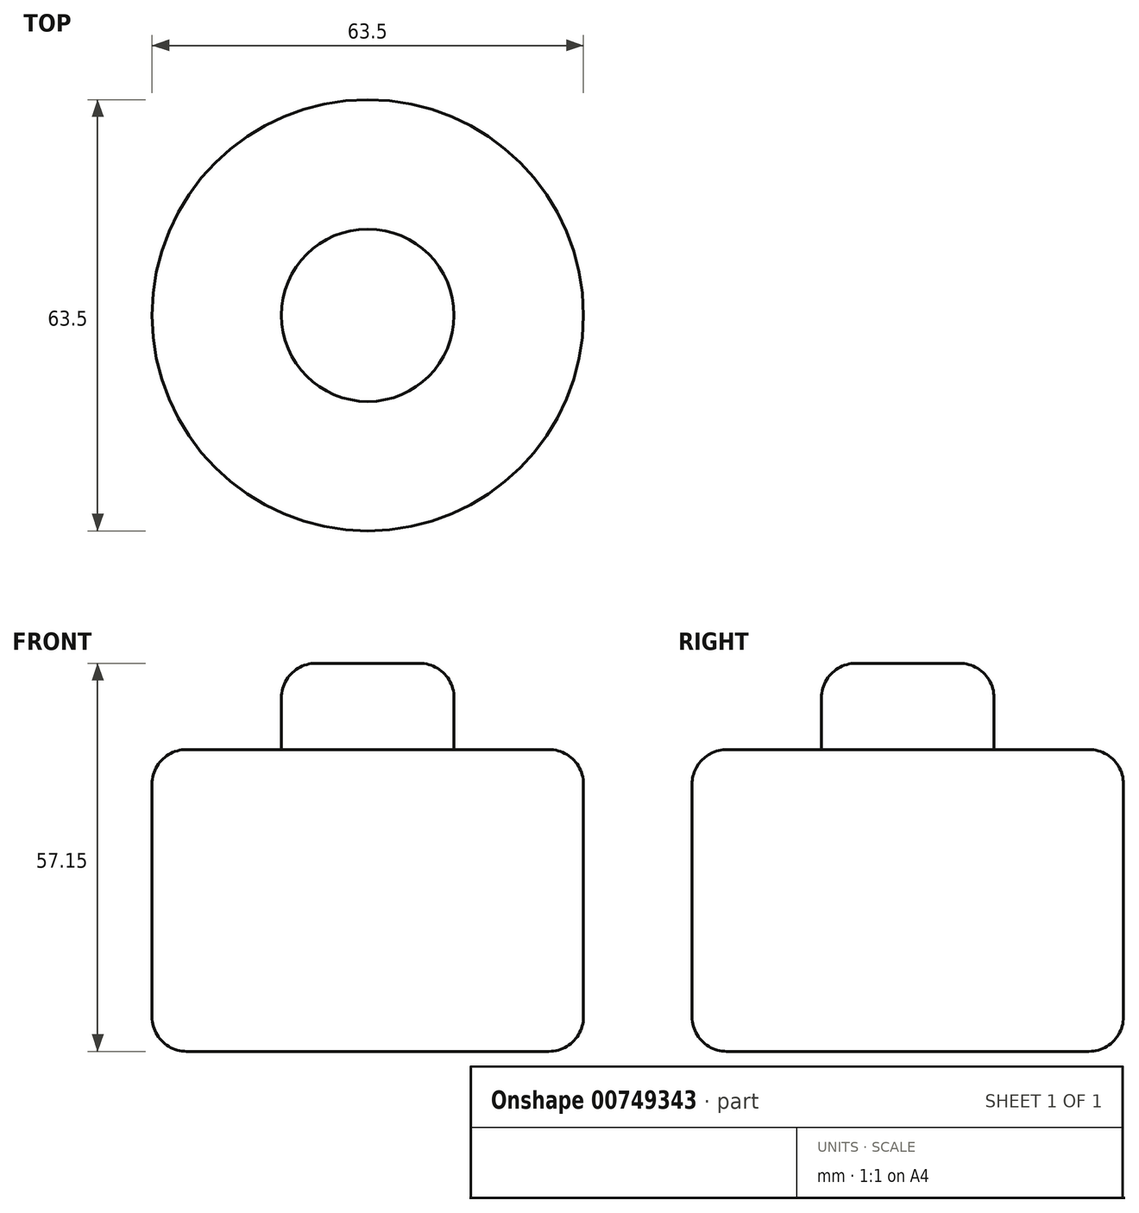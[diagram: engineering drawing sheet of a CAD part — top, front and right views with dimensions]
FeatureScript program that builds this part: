
annotation { "Feature Type Name" : "Feature", "Feature Type Description" : "" }
export const myFeature = defineFeature(function(context is Context, id is Id, definition is map)
    precondition{}
    {
        {
            var Q0;
            Q0=qCreatedBy(makeId("Top.planeOp"),FACE);
            var sketch = newSketch(context, id + "F0", { "sketchPlane" : qUnion([Q0])});
            skCircle(sketch, "E0", {"center": v(-9.3, 5.8) * mm, "radius": 31.75 * mm});
            skSolve(sketch);
        }
        {
            var Q0;
            Q0=makeQuery(id+"F0.imprint","IMPRINT",FACE,{"disambiguationData":[TD([[makeQuery(id+"F0.imprint","IMPRINT",EDGE,{"derivedFrom":sQuery(id+"F0.wireOp",EDGE,"E0")}),1.0]])]});
            extrude(context, id + "F1", {"entities" : qUnion([Q0]), "depth" : 44.45 * mm, "offsetDistance" : 25.4 * mm});
        }
        {
            var Q0;
            Q0=makeQuery(id+"F1.opExtrude","CAP_FACE",FACE,{"disambiguationData":[OSD([sQuery(id+"F0.wireOp",EDGE,"E0")])],"isStart":false});
            var sketch = newSketch(context, id + "F2", { "sketchPlane" : qUnion([Q0])});
            skCircle(sketch, "E1", {"center": v(-9.3, 5.8) * mm, "radius": 12.7 * mm});
            skSolve(sketch);
        }
        {
            var Q0;
            Q0=makeQuery(id+"F2.imprint","IMPRINT",FACE,{"disambiguationData":[TD([[makeQuery(id+"F2.imprint","IMPRINT",EDGE,{"derivedFrom":sQuery(id+"F2.wireOp",EDGE,"E1")}),1.0]])]});
            extrude(context, id + "F3", {"entities" : qUnion([Q0]), "operationType" : NewBodyOperationType.ADD, "depth" : 12.7 * mm, "offsetDistance" : 25.4 * mm});
        }
        {
            var Q0;
            Q0=makeQuery(id+"F1.opExtrude","CAP_EDGE",EDGE,{"disambiguationData":[OSD([sQuery(id+"F0.wireOp",EDGE,"E0")])],"isStart":false});
            var Q1;
            Q1=makeQuery(id+"F1.opExtrude","CAP_EDGE",EDGE,{"disambiguationData":[OSD([sQuery(id+"F0.wireOp",EDGE,"E0")])],"isStart":true});
            var Q2;
            Q2=makeQuery(id+"F3.opExtrude","CAP_EDGE",EDGE,{"disambiguationData":[OSD([sQuery(id+"F2.wireOp",EDGE,"E1")])],"isStart":false});
            fillet(context, id + "F4", {"entities" : qUnion([Q0, Q1, Q2]), "radius" : 5.08 * mm, "tangentPropagation" : true, "allowEdgeOverflow" : false});
        }
    });
